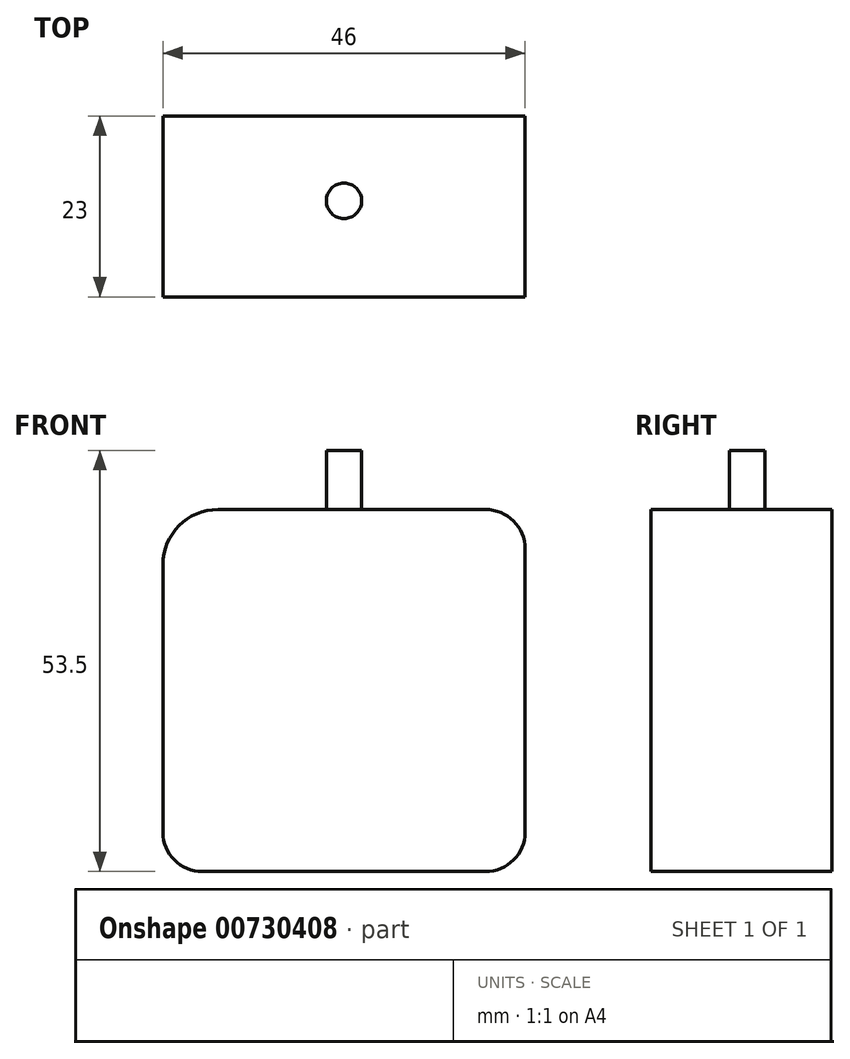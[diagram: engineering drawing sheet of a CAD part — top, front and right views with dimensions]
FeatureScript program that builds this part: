
annotation { "Feature Type Name" : "Feature", "Feature Type Description" : "" }
export const myFeature = defineFeature(function(context is Context, id is Id, definition is map)
    precondition{}
    {
        {
            var Q0;
            Q0=qCreatedBy(makeId("Front.planeOp"),FACE);
            var sketch = newSketch(context, id + "F0", { "sketchPlane" : qUnion([Q0])});
            skLineSegment(sketch, "E0.bottom", {"start": v(23, -23) * mm, "end": v(-23, -23) * mm});
            skLineSegment(sketch, "E0.top", {"start": v(23, 23) * mm, "end": v(-23, 23) * mm});
            skLineSegment(sketch, "E0.left", {"start": v(23, -23) * mm, "end": v(23, 23) * mm});
            skLineSegment(sketch, "E0.right", {"start": v(-23, -23) * mm, "end": v(-23, 23) * mm});
            skPoint(sketch, "E0.middle", {"position": v(0, 0) * mm});
            skSolve(sketch);
        }
        {
            var Q0;
            Q0=makeQuery(id+"F0.imprint","IMPRINT",FACE,{"disambiguationData":[TD([[makeQuery(id+"F0.imprint","IMPRINT",EDGE,{"derivedFrom":sQuery(id+"F0.wireOp",EDGE,"E0.bottom")}),-1.0]])]});
            extrude(context, id + "F1", {"entities" : qUnion([Q0]), "depth" : 23 * mm, "offsetDistance" : 25 * mm});
        }
        {
            var Q0;
            Q0=makeQuery(id+"F1.opExtrude","SWEPT_EDGE",EDGE,{"disambiguationData":[OSD([sQuery(id+"F0.wireOp",EDGE,"E0.top"),sQuery(id+"F0.wireOp",EDGE,"E0.right")])]});
            fillet(context, id + "F2", {"entities" : qUnion([Q0]), "radius" : 7 * mm, "tangentPropagation" : true, "allowEdgeOverflow" : false});
        }
        {
            var Q0;
            Q0=makeQuery(id+"F1.opExtrude","SWEPT_EDGE",EDGE,{"disambiguationData":[OSD([sQuery(id+"F0.wireOp",EDGE,"E0.top"),sQuery(id+"F0.wireOp",EDGE,"E0.left")])]});
            var Q1;
            Q1=makeQuery(id+"F1.opExtrude","SWEPT_EDGE",EDGE,{"disambiguationData":[OSD([sQuery(id+"F0.wireOp",EDGE,"E0.bottom"),sQuery(id+"F0.wireOp",EDGE,"E0.left")])]});
            var Q2;
            Q2=makeQuery(id+"F1.opExtrude","SWEPT_EDGE",EDGE,{"disambiguationData":[OSD([sQuery(id+"F0.wireOp",EDGE,"E0.bottom"),sQuery(id+"F0.wireOp",EDGE,"E0.right")])]});
            fillet(context, id + "F3", {"entities" : qUnion([Q0, Q1, Q2]), "radius" : 5 * mm, "tangentPropagation" : true, "allowEdgeOverflow" : false});
        }
        {
            var Q0;
            Q0=makeQuery(id+"F1.opExtrude","SWEPT_FACE",FACE,{"disambiguationData":[OSD([sQuery(id+"F0.wireOp",EDGE,"E0.top")])]});
            var sketch = newSketch(context, id + "F4", { "sketchPlane" : qUnion([Q0])});
            skCircle(sketch, "E1", {"center": v(0, -10.78) * mm, "radius": 2.25 * mm});
            skSolve(sketch);
        }
        {
            var Q0;
            Q0 = qSketchRegion(id + "F4", true);
            extrude(context, id + "F5", {"entities" : qUnion([Q0]), "operationType" : NewBodyOperationType.ADD, "depth" : 7.5 * mm, "offsetDistance" : 25 * mm});
        }
    });
